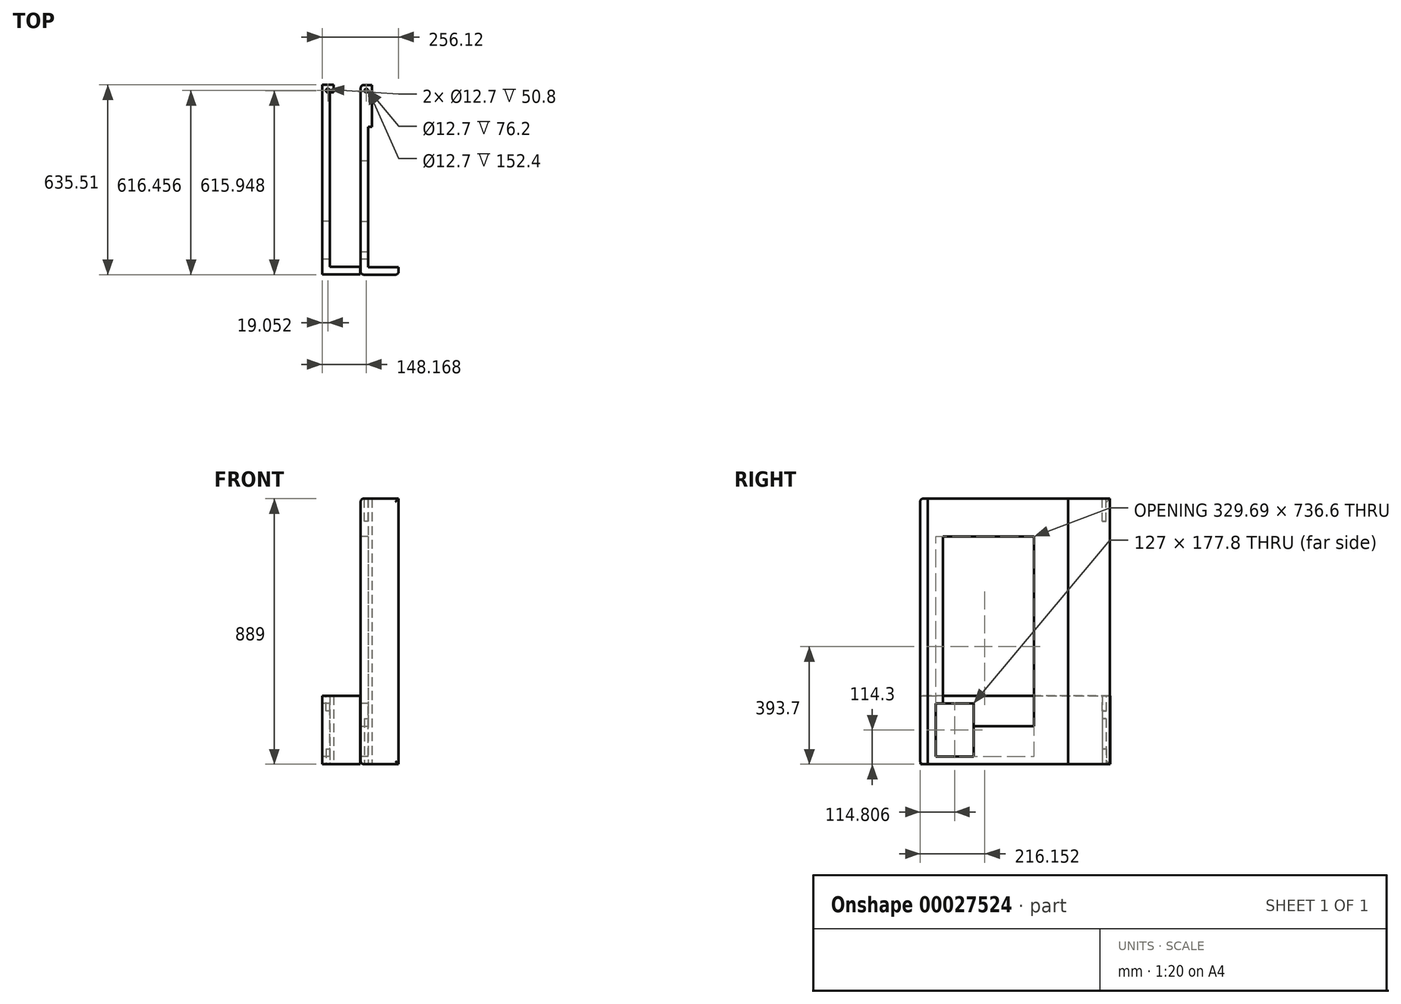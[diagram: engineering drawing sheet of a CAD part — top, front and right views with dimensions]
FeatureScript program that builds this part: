
annotation { "Feature Type Name" : "Feature", "Feature Type Description" : "" }
export const myFeature = defineFeature(function(context is Context, id is Id, definition is map)
    precondition{}
    {
        {
            var Q0;
            Q0=qCreatedBy(makeId("Top.planeOp"),FACE);
            var sketch = newSketch(context, id + "F0", { "sketchPlane" : qUnion([Q0])});
            skLineSegment(sketch, "E0", {"start": v(-83.65, 411.49) * mm, "end": v(-121.75, 411.49) * mm});
            skLineSegment(sketch, "E1", {"start": v(-121.75, 411.49) * mm, "end": v(-121.75, -223.51) * mm});
            skLineSegment(sketch, "E2", {"start": v(-121.75, -223.51) * mm, "end": v(5.25, -223.51) * mm});
            skLineSegment(sketch, "E3", {"start": v(5.25, -223.51) * mm, "end": v(5.25, -198.11) * mm});
            skLineSegment(sketch, "E4", {"start": v(5.25, -198.11) * mm, "end": v(-96.35, -198.11) * mm});
            skLineSegment(sketch, "E5", {"start": v(-96.35, -198.11) * mm, "end": v(-96.35, 271.79) * mm});
            skLineSegment(sketch, "E6", {"start": v(-96.35, 271.79) * mm, "end": v(-83.65, 271.79) * mm});
            skLineSegment(sketch, "E7", {"start": v(-83.65, 411.49) * mm, "end": v(-83.65, 271.79) * mm});
            skSolve(sketch);
        }
        {
            var Q0;
            Q0=makeQuery(id+"F0.imprint","IMPRINT",FACE,{"disambiguationData":[TD([[makeQuery(id+"F0.imprint","IMPRINT",EDGE,{"derivedFrom":sQuery(id+"F0.wireOp",EDGE,"E0")}),1.0]])]});
            extrude(context, id + "F1", {"entities" : qUnion([Q0]), "depth" : 889 * mm});
        }
        {
            var Q0;
            Q0=makeQuery(id+"F1.opExtrude","SWEPT_FACE",FACE,{"disambiguationData":[OSD([sQuery(id+"F0.wireOp",EDGE,"E1")])]});
            var sketch = newSketch(context, id + "F2", { "sketchPlane" : qUnion([Q0])});
            skLineSegment(sketch, "E8.bottom", {"start": v(147.31, 762) * mm, "end": v(-157.49, 762) * mm});
            skLineSegment(sketch, "E8.top", {"start": v(147.31, 127) * mm, "end": v(-157.49, 127) * mm});
            skLineSegment(sketch, "E8.left", {"start": v(147.31, 762) * mm, "end": v(147.31, 127) * mm});
            skLineSegment(sketch, "E8.right", {"start": v(-157.49, 762) * mm, "end": v(-157.49, 127) * mm});
            skSolve(sketch);
        }
        {
            var Q0;
            Q0=makeQuery(id+"F2.imprint","IMPRINT",FACE,{"disambiguationData":[TD([[makeQuery(id+"F2.imprint","IMPRINT",EDGE,{"derivedFrom":sQuery(id+"F2.wireOp",EDGE,"E8.bottom")}),1.0]])]});
            extrude(context, id + "F3", {"entities" : qUnion([Q0]), "operationType" : NewBodyOperationType.REMOVE, "endBound" : BoundingType.THROUGH_ALL, "oppositeDirection" : true, "depth" : 25.4 * mm});
        }
        {
            var Q0;
            Q0=makeQuery(id+"F1.opExtrude","CAP_FACE",FACE,{"disambiguationData":[OSD([sQuery(id+"F0.wireOp",EDGE,"E0"),sQuery(id+"F0.wireOp",EDGE,"E1"),sQuery(id+"F0.wireOp",EDGE,"E2"),sQuery(id+"F0.wireOp",EDGE,"E3"),sQuery(id+"F0.wireOp",EDGE,"E4"),sQuery(id+"F0.wireOp",EDGE,"E5"),sQuery(id+"F0.wireOp",EDGE,"E6"),sQuery(id+"F0.wireOp",EDGE,"E7")])],"isStart":false});
            var sketch = newSketch(context, id + "F4", { "sketchPlane" : qUnion([Q0])});
            skCircle(sketch, "E9", {"center": v(-102.7, 392.44) * mm, "radius": 6.35 * mm});
            skSolve(sketch);
        }
        {
            var Q0;
            Q0=makeQuery(id+"F4.imprint","IMPRINT",FACE,{"disambiguationData":[TD([[makeQuery(id+"F4.imprint","IMPRINT",EDGE,{"derivedFrom":sQuery(id+"F4.wireOp",EDGE,"E9")}),1.0]])]});
            extrude(context, id + "F5", {"entities" : qUnion([Q0]), "operationType" : NewBodyOperationType.REMOVE, "oppositeDirection" : true, "depth" : 76.2 * mm});
        }
        {
            var Q0;
            Q0=makeQuery(id+"F1.opExtrude","CAP_FACE",FACE,{"disambiguationData":[OSD([sQuery(id+"F0.wireOp",EDGE,"E0"),sQuery(id+"F0.wireOp",EDGE,"E1"),sQuery(id+"F0.wireOp",EDGE,"E2"),sQuery(id+"F0.wireOp",EDGE,"E3"),sQuery(id+"F0.wireOp",EDGE,"E4"),sQuery(id+"F0.wireOp",EDGE,"E5"),sQuery(id+"F0.wireOp",EDGE,"E6"),sQuery(id+"F0.wireOp",EDGE,"E7")])],"isStart":true});
            var sketch = newSketch(context, id + "F6", { "sketchPlane" : qUnion([Q0])});
            skCircle(sketch, "E10", {"center": v(-102.7, -392.44) * mm, "radius": 6.35 * mm});
            skSolve(sketch);
        }
        {
            var Q0;
            Q0=makeQuery(id+"F6.imprint","IMPRINT",FACE,{"disambiguationData":[TD([[makeQuery(id+"F6.imprint","IMPRINT",EDGE,{"derivedFrom":sQuery(id+"F6.wireOp",EDGE,"E10")}),1.0]])]});
            extrude(context, id + "F7", {"entities" : qUnion([Q0]), "operationType" : NewBodyOperationType.REMOVE, "oppositeDirection" : true, "depth" : 152.4 * mm});
        }
        {
            var Q0;
            Q0=makeQuery(id+"F1.opExtrude","CAP_EDGE",EDGE,{"disambiguationData":[OSD([sQuery(id+"F0.wireOp",EDGE,"E1")])],"isStart":true});
            var Q1;
            Q1=makeQuery(id+"F1.opExtrude","SWEPT_EDGE",EDGE,{"disambiguationData":[OSD([sQuery(id+"F0.wireOp",EDGE,"E0"),sQuery(id+"F0.wireOp",EDGE,"E1")])]});
            var Q2;
            Q2=makeQuery(id+"F1.opExtrude","CAP_EDGE",EDGE,{"disambiguationData":[OSD([sQuery(id+"F0.wireOp",EDGE,"E2")])],"isStart":true});
            var Q3;
            Q3=makeQuery(id+"F1.opExtrude","CAP_EDGE",EDGE,{"disambiguationData":[OSD([sQuery(id+"F0.wireOp",EDGE,"E2")])],"isStart":false});
            var Q4;
            Q4=makeQuery(id+"F1.opExtrude","CAP_EDGE",EDGE,{"disambiguationData":[OSD([sQuery(id+"F0.wireOp",EDGE,"E1")])],"isStart":false});
            var Q5;
            Q5=makeQuery(id+"F3.boolean.opBoolean","COPY",EDGE,{"derivedFrom":makeQuery(id+"F3.opExtrude","CAP_EDGE",EDGE,{"disambiguationData":[OSD([sQuery(id+"F2.wireOp",EDGE,"E8.right")])],"isStart":true})});
            var Q6;
            Q6=makeQuery(id+"F3.boolean.opBoolean","COPY",EDGE,{"derivedFrom":makeQuery(id+"F3.opExtrude","CAP_EDGE",EDGE,{"disambiguationData":[OSD([sQuery(id+"F2.wireOp",EDGE,"E8.bottom")])],"isStart":true})});
            var Q7;
            Q7=makeQuery(id+"F3.boolean.opBoolean","COPY",EDGE,{"derivedFrom":makeQuery(id+"F3.opExtrude","CAP_EDGE",EDGE,{"disambiguationData":[OSD([sQuery(id+"F2.wireOp",EDGE,"E8.left")])],"isStart":true})});
            var Q8;
            Q8=makeQuery(id+"F1.opExtrude","SWEPT_EDGE",EDGE,{"disambiguationData":[OSD([sQuery(id+"F0.wireOp",EDGE,"E1"),sQuery(id+"F0.wireOp",EDGE,"E2")])]});
            var Q9;
            Q9=makeQuery(id+"F1.opExtrude","SWEPT_EDGE",EDGE,{"disambiguationData":[OSD([sQuery(id+"F0.wireOp",EDGE,"E2"),sQuery(id+"F0.wireOp",EDGE,"E3")])]});
            var Q10;
            Q10=makeQuery(id+"F3.boolean.opBoolean","COPY",EDGE,{"derivedFrom":makeQuery(id+"F3.opExtrude","CAP_EDGE",EDGE,{"disambiguationData":[OSD([sQuery(id+"F2.wireOp",EDGE,"E8.top")])],"isStart":true})});
            fillet(context, id + "F8", {"entities" : qUnion([Q0, Q1, Q2, Q3, Q4, Q5, Q6, Q7, Q8, Q9, Q10]), "radius" : 10.16 * mm, "tangentPropagation" : true, "allowEdgeOverflow" : false});
        }
        {
            var Q0;
            Q0=qCreatedBy(makeId("Top.planeOp"),FACE);
            var sketch = newSketch(context, id + "F9", { "sketchPlane" : qUnion([Q0])});
            skLineSegment(sketch, "E11", {"start": v(-250.87, 412) * mm, "end": v(-250.87, -223) * mm});
            skLineSegment(sketch, "E12", {"start": v(-250.87, -223) * mm, "end": v(-123.87, -223) * mm});
            skLineSegment(sketch, "E13", {"start": v(-123.87, -223) * mm, "end": v(-123.87, -197.6) * mm});
            skLineSegment(sketch, "E14", {"start": v(-123.87, -197.6) * mm, "end": v(-225.47, -197.6) * mm});
            skLineSegment(sketch, "E15", {"start": v(-225.47, -197.6) * mm, "end": v(-225.47, 386.6) * mm});
            skLineSegment(sketch, "E16", {"start": v(-225.47, 386.6) * mm, "end": v(-212.77, 386.6) * mm});
            skLineSegment(sketch, "E17", {"start": v(-212.77, 386.6) * mm, "end": v(-212.77, 412) * mm});
            skLineSegment(sketch, "E18", {"start": v(-212.77, 412) * mm, "end": v(-250.87, 412) * mm});
            skSolve(sketch);
        }
        {
            var Q0;
            Q0=makeQuery(id+"F9.imprint","IMPRINT",FACE,{"disambiguationData":[TD([[makeQuery(id+"F9.imprint","IMPRINT",EDGE,{"derivedFrom":sQuery(id+"F9.wireOp",EDGE,"E11")}),1.0]])]});
            extrude(context, id + "F10", {"entities" : qUnion([Q0]), "depth" : 228.6 * mm});
        }
        {
            var Q0;
            Q0=makeQuery(id+"F10.opExtrude","SWEPT_FACE",FACE,{"disambiguationData":[OSD([sQuery(id+"F9.wireOp",EDGE,"E11")])]});
            var sketch = newSketch(context, id + "F11", { "sketchPlane" : qUnion([Q0])});
            skLineSegment(sketch, "E19.bottom", {"start": v(45.2, 25.4) * mm, "end": v(172.2, 25.4) * mm});
            skLineSegment(sketch, "E19.top", {"start": v(45.2, 203.2) * mm, "end": v(172.2, 203.2) * mm});
            skLineSegment(sketch, "E19.left", {"start": v(45.2, 25.4) * mm, "end": v(45.2, 203.2) * mm});
            skLineSegment(sketch, "E19.right", {"start": v(172.2, 25.4) * mm, "end": v(172.2, 203.2) * mm});
            skSolve(sketch);
        }
        {
            var Q0;
            Q0=makeQuery(id+"F11.imprint","IMPRINT",FACE,{"disambiguationData":[TD([[makeQuery(id+"F11.imprint","IMPRINT",EDGE,{"derivedFrom":sQuery(id+"F11.wireOp",EDGE,"E19.bottom")}),1.0]])]});
            extrude(context, id + "F12", {"entities" : qUnion([Q0]), "operationType" : NewBodyOperationType.REMOVE, "endBound" : BoundingType.THROUGH_ALL, "oppositeDirection" : true, "depth" : 25.4 * mm});
        }
        {
            var Q0;
            Q0=makeQuery(id+"F10.opExtrude","CAP_FACE",FACE,{"disambiguationData":[OSD([sQuery(id+"F9.wireOp",EDGE,"E11"),sQuery(id+"F9.wireOp",EDGE,"E12"),sQuery(id+"F9.wireOp",EDGE,"E13"),sQuery(id+"F9.wireOp",EDGE,"E14"),sQuery(id+"F9.wireOp",EDGE,"E15"),sQuery(id+"F9.wireOp",EDGE,"E16"),sQuery(id+"F9.wireOp",EDGE,"E17"),sQuery(id+"F9.wireOp",EDGE,"E18")])],"isStart":true});
            var sketch = newSketch(context, id + "F13", { "sketchPlane" : qUnion([Q0])});
            skCircle(sketch, "E20", {"center": v(-231.82, -392.95) * mm, "radius": 6.35 * mm});
            skSolve(sketch);
        }
        {
            var Q0;
            Q0=makeQuery(id+"F13.imprint","IMPRINT",FACE,{"disambiguationData":[TD([[makeQuery(id+"F13.imprint","IMPRINT",EDGE,{"derivedFrom":sQuery(id+"F13.wireOp",EDGE,"E20")}),1.0]])]});
            var Q1;
            Q1=sQuery(id+"F13.wireOp",EDGE,"E20");
            extrude(context, id + "F14", {"entities" : qUnion([Q0]), "operationType" : NewBodyOperationType.REMOVE, "surfaceEntities" : qUnion([Q1]), "oppositeDirection" : true, "depth" : 50.8 * mm});
        }
        {
            var Q0;
            Q0=makeQuery(id+"F10.opExtrude","CAP_FACE",FACE,{"disambiguationData":[OSD([sQuery(id+"F9.wireOp",EDGE,"E11"),sQuery(id+"F9.wireOp",EDGE,"E12"),sQuery(id+"F9.wireOp",EDGE,"E13"),sQuery(id+"F9.wireOp",EDGE,"E14"),sQuery(id+"F9.wireOp",EDGE,"E15"),sQuery(id+"F9.wireOp",EDGE,"E16"),sQuery(id+"F9.wireOp",EDGE,"E17"),sQuery(id+"F9.wireOp",EDGE,"E18")])],"isStart":false});
            var sketch = newSketch(context, id + "F15", { "sketchPlane" : qUnion([Q0])});
            skCircle(sketch, "E21", {"center": v(-231.82, 392.95) * mm, "radius": 6.35 * mm});
            skSolve(sketch);
        }
        {
            var Q0;
            Q0=makeQuery(id+"F15.imprint","IMPRINT",FACE,{"disambiguationData":[TD([[makeQuery(id+"F15.imprint","IMPRINT",EDGE,{"derivedFrom":sQuery(id+"F15.wireOp",EDGE,"E21")}),1.0]])]});
            extrude(context, id + "F16", {"entities" : qUnion([Q0]), "operationType" : NewBodyOperationType.REMOVE, "oppositeDirection" : true, "depth" : 50.8 * mm});
        }
    });
